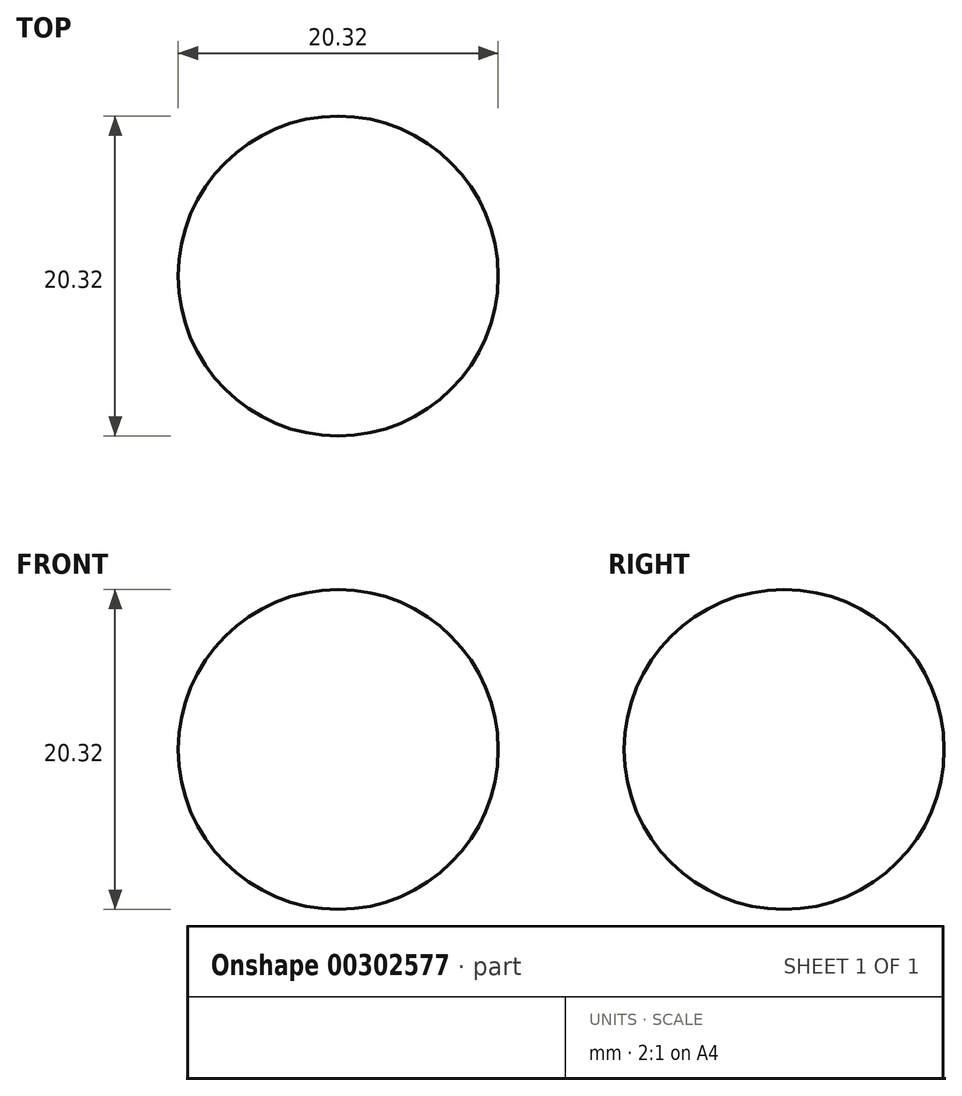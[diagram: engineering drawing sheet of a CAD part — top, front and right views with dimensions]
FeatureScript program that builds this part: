
annotation { "Feature Type Name" : "Feature", "Feature Type Description" : "" }
export const myFeature = defineFeature(function(context is Context, id is Id, definition is map)
    precondition{}
    {
        {
            var Q0;
            Q0=qCreatedBy(makeId("Front.planeOp"),FACE);
            var sketch = newSketch(context, id + "F0", { "sketchPlane" : qUnion([Q0])});
            skLineSegment(sketch, "E0", {"start": v(0, 0) * mm, "end": v(0, 20.32) * mm});
            skArc(sketch, "E1", {"start": v(0, 0) * mm, "mid": v(10.16, 10.16) * mm, "end": v(0, 20.32) * mm});
            skLineSegment(sketch, "E2", {"start": v(0, 31.02) * mm, "end": v(0, -23.08) * mm, "construction": true});
            skSolve(sketch);
        }
        {
            var Q0;
            Q0=makeQuery(id+"F0.imprint","IMPRINT",FACE,{"disambiguationData":[TD([[makeQuery(id+"F0.imprint","IMPRINT",EDGE,{"derivedFrom":sQuery(id+"F0.wireOp",EDGE,"E0")}),-1.0]])]});
            var Q1;
            Q1=sQuery(id+"F0.wireOp",EDGE,"E2");
            revolve(context, id + "F1", {"entities" : qUnion([Q0]), "axis" : qUnion([Q1]), "revolveType" : RevolveType.FULL});
        }
    });
